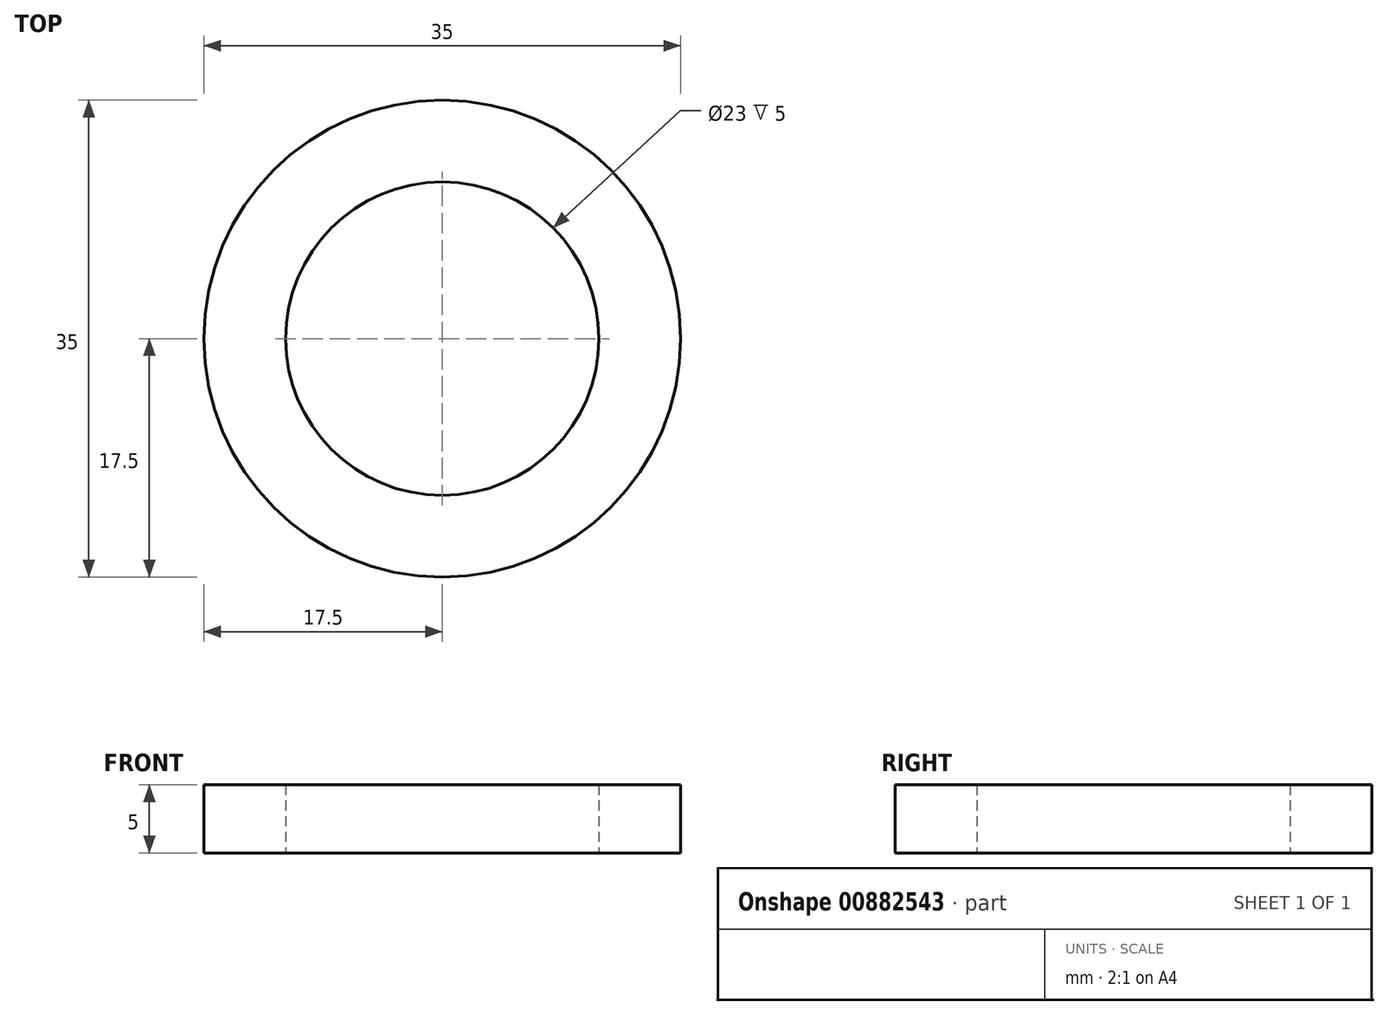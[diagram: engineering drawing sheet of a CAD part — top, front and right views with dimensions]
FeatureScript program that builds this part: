
annotation { "Feature Type Name" : "Feature", "Feature Type Description" : "" }
export const myFeature = defineFeature(function(context is Context, id is Id, definition is map)
    precondition{}
    {
        {
            var Q0;
            Q0=qCreatedBy(makeId("Top.planeOp"),FACE);
            var sketch = newSketch(context, id + "F0", { "sketchPlane" : qUnion([Q0])});
            skCircle(sketch, "E0", {"center": v(0, 0) * mm, "radius": 11.5 * mm});
            skCircle(sketch, "E1", {"center": v(0, 0) * mm, "radius": 17.5 * mm});
            skSolve(sketch);
        }
        {
            var Q0;
            Q0 = qSketchRegion(id + "F0", true);
            extrude(context, id + "F1", {"entities" : qUnion([Q0]), "depth" : 5 * mm, "offsetDistance" : 25 * mm});
        }
    });
